# Revit family: Storage-Freestanding-Teknion-BCFSO-Freestanding_Open_Tower-R2015
name_source: partatom
category: Furniture
revit_build: Autodesk Revit Architecture 2015 (Build: 20140323_1530(x64)
units: mm (PartAtom-declared; Revit-internal decimal feet)

## types (2) — shared parameters
Actual Depth = 17.161 "
Assembly Code = E2020200
Depth = 18 "
Manufacturer = Teknion
Manufacturer Fax = 416.661.4586
Part Number = BCFSO
Product Documentation Link = http://www.teknion.com
Product Line = Expansion Casegoods
Product Page URL = http://www.teknion.com
Series = Expansion Casegoods
Sustainability Data = http://www.teknion.com
URL = www.teknion.com
Unit Weight URL = http://www.teknion.com
Warranty = http://www.teknion.com

## per-type parameters (varying)
| type | 72 High | Actual Height | Description | Height | Model | Shelf Offset Row 1 | Shelf Offset Row 2 | Shelf Offset Row 3 |
| 66" High | No | 65.165 " | Freestanding Open Tower, 18"Depth, 66" High | 66 " | BCFSO18_66 | 14.846 " | 15.197 " | 14.906 " |
| 72" High | Yes | 71.406 " | Freestanding Open Tower, 18"Depth, 72" High | 72 " | BCFSO18_72 | 16.927 " | 17.277 " | 16.986 " |

## geometry (parser evidence)
native form markers: Blend x46, Sweep x2
no freeform markers — native parametric forms only
